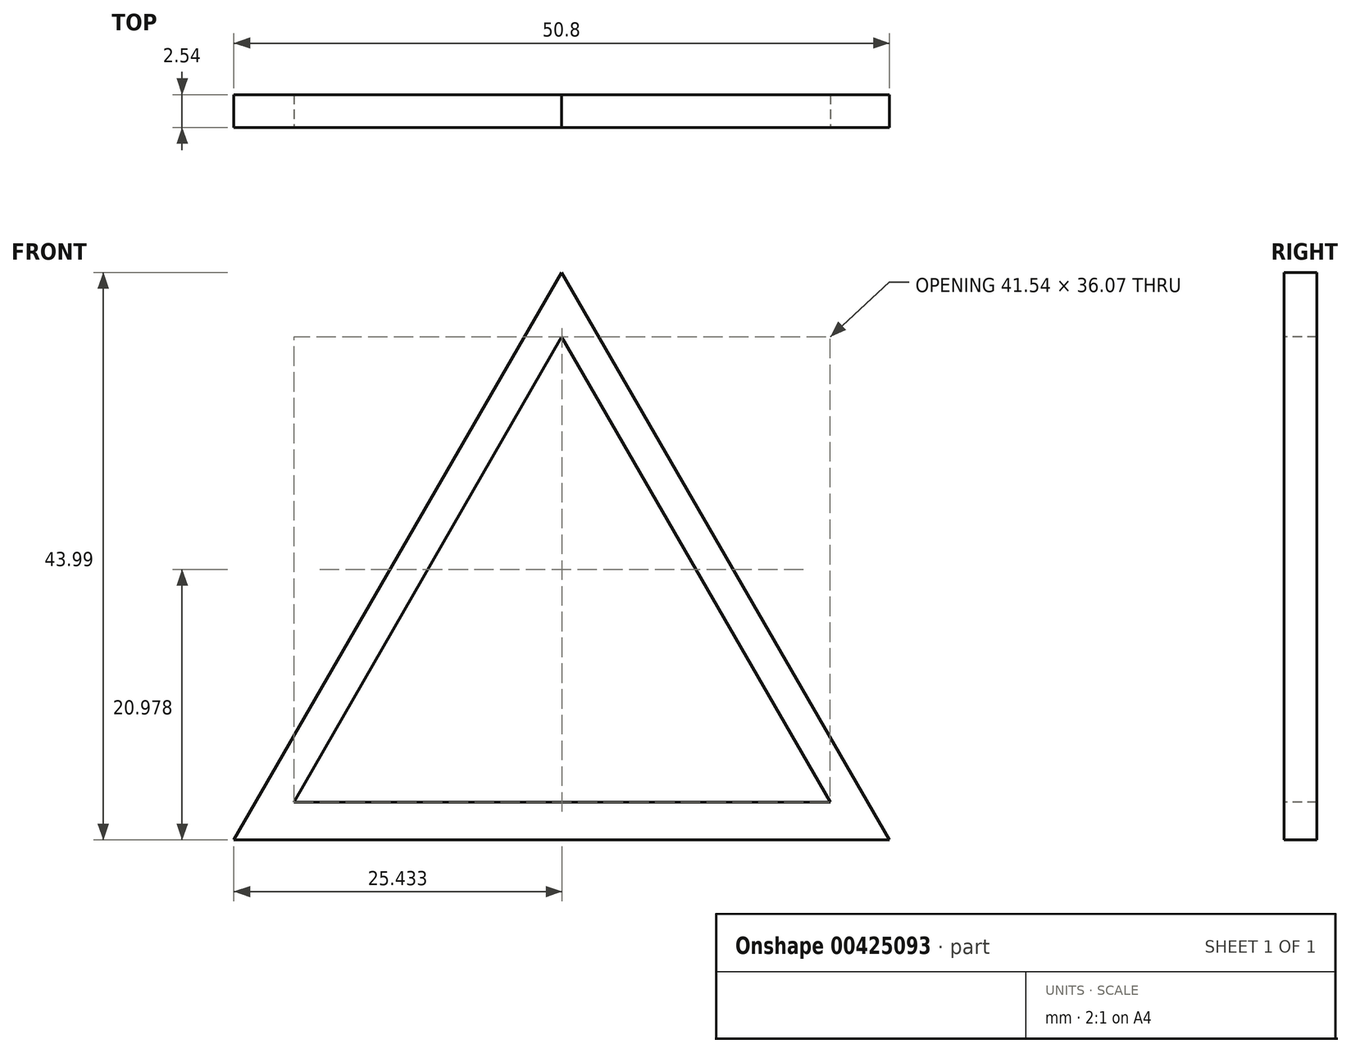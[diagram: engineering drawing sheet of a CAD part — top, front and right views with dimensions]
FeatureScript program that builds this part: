
annotation { "Feature Type Name" : "Feature", "Feature Type Description" : "" }
export const myFeature = defineFeature(function(context is Context, id is Id, definition is map)
    precondition{}
    {
        {
            var Q0;
            Q0=qCreatedBy(makeId("Front.planeOp"),FACE);
            var sketch = newSketch(context, id + "F0", { "sketchPlane" : qUnion([Q0])});
            skLineSegment(sketch, "E0", {"start": v(-83.4, 0) * mm, "end": v(-58, 44) * mm});
            skLineSegment(sketch, "E1", {"start": v(-58, 44) * mm, "end": v(-32.6, 0) * mm});
            skLineSegment(sketch, "E2", {"start": v(-32.6, 0) * mm, "end": v(-83.4, 0) * mm});
            skSolve(sketch);
        }
        {
            var Q0;
            Q0=makeQuery(id+"F0.imprint","IMPRINT",FACE,{"disambiguationData":[TD([[makeQuery(id+"F0.imprint","IMPRINT",EDGE,{"derivedFrom":sQuery(id+"F0.wireOp",EDGE,"E0")}),-1.0]])]});
            extrude(context, id + "F1", {"entities" : qUnion([Q0]), "depth" : 2.54 * mm});
        }
        {
            var Q0;
            Q0=makeQuery(id+"F1.opExtrude","CAP_FACE",FACE,{"disambiguationData":[OSD([sQuery(id+"F0.wireOp",EDGE,"E0"),sQuery(id+"F0.wireOp",EDGE,"E1"),sQuery(id+"F0.wireOp",EDGE,"E2")])],"isStart":false});
            var sketch = newSketch(context, id + "F2", { "sketchPlane" : qUnion([Q0])});
            skLineSegment(sketch, "E3", {"start": v(-58.03, 39.01) * mm, "end": v(-37.2, 2.94) * mm});
            skLineSegment(sketch, "E4", {"start": v(-37.2, 2.94) * mm, "end": v(-78.75, 2.94) * mm});
            skLineSegment(sketch, "E5", {"start": v(-78.75, 2.94) * mm, "end": v(-58.03, 39.01) * mm});
            skSolve(sketch);
        }
        {
            var Q0;
            Q0 = qSketchRegion(id + "F2", true);
            extrude(context, id + "F3", {"entities" : qUnion([Q0]), "operationType" : NewBodyOperationType.REMOVE, "oppositeDirection" : true, "depth" : 25.4 * mm});
        }
    });
